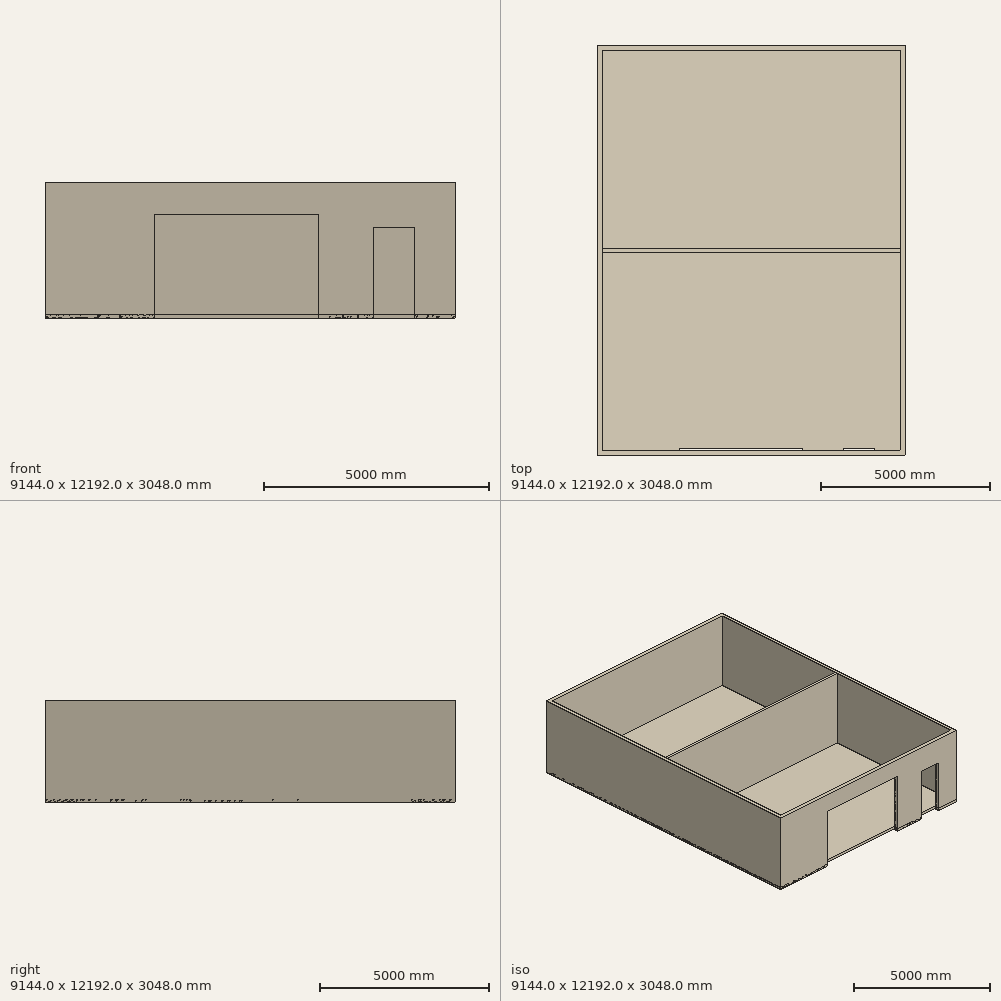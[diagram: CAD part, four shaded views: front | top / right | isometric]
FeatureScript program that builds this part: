
annotation { "Feature Type Name" : "Feature", "Feature Type Description" : "" }
export const myFeature = defineFeature(function(context is Context, id is Id, definition is map)
    precondition{}
    {
        {
            var Q0;
            Q0=qCreatedBy(makeId("Top.planeOp"),FACE);
            var sketch = newSketch(context, id + "F0", { "sketchPlane" : qUnion([Q0])});
            skLineSegment(sketch, "E0.bottom", {"start": v(-4572, 6096) * mm, "end": v(4572, 6096) * mm});
            skLineSegment(sketch, "E0.top", {"start": v(-4572, -6096) * mm, "end": v(4572, -6096) * mm});
            skLineSegment(sketch, "E0.left", {"start": v(-4572, 6096) * mm, "end": v(-4572, -6096) * mm});
            skLineSegment(sketch, "E0.right", {"start": v(4572, 6096) * mm, "end": v(4572, -6096) * mm});
            skLineSegment(sketch, "E1", {"start": v(0, 0) * mm, "end": v(0, 6096) * mm, "construction": true});
            skLineSegment(sketch, "E2", {"start": v(0, 0) * mm, "end": v(4572, 0) * mm, "construction": true});
            skLineSegment(sketch, "E3.0", {"start": v(4419.6, 5943.6) * mm, "end": v(4419.6, -5943.6) * mm});
            skLineSegment(sketch, "E3.1", {"start": v(-4419.6, 5943.6) * mm, "end": v(4419.6, 5943.6) * mm});
            skLineSegment(sketch, "E3.2", {"start": v(-4419.6, 5943.6) * mm, "end": v(-4419.6, -5943.6) * mm});
            skLineSegment(sketch, "E3.3", {"start": v(-4419.6, -5943.6) * mm, "end": v(4419.6, -5943.6) * mm});
            skSolve(sketch);
        }
        {
            var Q0;
            Q0 = qSketchRegion(id + "F0", true);
            var Q1;
            Q1=makeQuery(id+"F0.imprint","IMPRINT",FACE,{"disambiguationData":[TD([[makeQuery(id+"F0.imprint","IMPRINT",EDGE,{"derivedFrom":sQuery(id+"F0.wireOp",EDGE,"E3.0")}),-1.0]])]});
            extrude(context, id + "F1", {"entities" : qUnion([Q0, Q1]), "depth" : 101.6 * mm, "offsetDistance" : 25.4 * mm});
        }
        {
            var Q0;
            Q0 = qSketchRegion(id + "F0", true);
            extrude(context, id + "F2", {"entities" : qUnion([Q0]), "depth" : 3048 * mm, "offsetDistance" : 25.4 * mm});
        }
        {
            var Q0;
            Q0=makeQuery(id+"F1.opExtrude","CAP_FACE",FACE,{"disambiguationData":[OSD([sQuery(id+"F0.wireOp",EDGE,"E0.bottom"),sQuery(id+"F0.wireOp",EDGE,"E0.top"),sQuery(id+"F0.wireOp",EDGE,"E0.left"),sQuery(id+"F0.wireOp",EDGE,"E0.right")])],"isStart":false});
            var sketch = newSketch(context, id + "F3", { "sketchPlane" : qUnion([Q0])});
            skLineSegment(sketch, "E4.bottom", {"start": v(-4419.6, 50.8) * mm, "end": v(4419.6, 50.8) * mm});
            skLineSegment(sketch, "E4.top", {"start": v(-4419.6, -50.8) * mm, "end": v(4419.6, -50.8) * mm});
            skLineSegment(sketch, "E4.left", {"start": v(-4419.6, 50.8) * mm, "end": v(-4419.6, -50.8) * mm});
            skLineSegment(sketch, "E4.right", {"start": v(4419.6, 50.8) * mm, "end": v(4419.6, -50.8) * mm});
            skSolve(sketch);
        }
        {
            var Q0;
            Q0 = qSketchRegion(id + "F3", true);
            var Q1;
            Q1=makeQuery(id+"F2.opExtrude","CAP_FACE",FACE,{"disambiguationData":[OSD([sQuery(id+"F0.wireOp",EDGE,"E0.bottom"),sQuery(id+"F0.wireOp",EDGE,"E0.top"),sQuery(id+"F0.wireOp",EDGE,"E0.left"),sQuery(id+"F0.wireOp",EDGE,"E0.right"),sQuery(id+"F0.wireOp",EDGE,"E3.0"),sQuery(id+"F0.wireOp",EDGE,"E3.1"),sQuery(id+"F0.wireOp",EDGE,"E3.2"),sQuery(id+"F0.wireOp",EDGE,"E3.3")])],"isStart":false});
            extrude(context, id + "F4", {"entities" : qUnion([Q0]), "endBound" : BoundingType.UP_TO_SURFACE, "depth" : 25.4 * mm, "endBoundEntityFace" : qUnion([Q1]), "offsetDistance" : 25.4 * mm});
        }
        {
            var Q0;
            Q0=makeQuery(id+"F2.opExtrude","SWEPT_FACE",FACE,{"disambiguationData":[OSD([sQuery(id+"F0.wireOp",EDGE,"E0.top")])]});
            var sketch = newSketch(context, id + "F5", { "sketchPlane" : qUnion([Q0])});
            skLineSegment(sketch, "E5.bottom", {"start": v(-2133.6, 2336.8) * mm, "end": v(1524, 2336.8) * mm});
            skLineSegment(sketch, "E5.top", {"start": v(-2133.6, -101.6) * mm, "end": v(1524, -101.6) * mm});
            skLineSegment(sketch, "E5.left", {"start": v(-2133.6, 2336.8) * mm, "end": v(-2133.6, -101.6) * mm});
            skLineSegment(sketch, "E5.right", {"start": v(1524, 2336.8) * mm, "end": v(1524, -101.6) * mm});
            skLineSegment(sketch, "E6.bottom", {"start": v(2743.2, -101.6) * mm, "end": v(3657.6, -101.6) * mm});
            skLineSegment(sketch, "E6.top", {"start": v(2743.2, 2032) * mm, "end": v(3657.6, 2032) * mm});
            skLineSegment(sketch, "E6.left", {"start": v(2743.2, -101.6) * mm, "end": v(2743.2, 2032) * mm});
            skLineSegment(sketch, "E6.right", {"start": v(3657.6, -101.6) * mm, "end": v(3657.6, 2032) * mm});
            skSolve(sketch);
        }
        {
            var Q0;
            Q0 = qSketchRegion(id + "F5", true);
            extrude(context, id + "F6", {"entities" : qUnion([Q0]), "operationType" : NewBodyOperationType.REMOVE, "oppositeDirection" : true, "depth" : 203.2 * mm, "offsetDistance" : 25.4 * mm});
        }
    });
